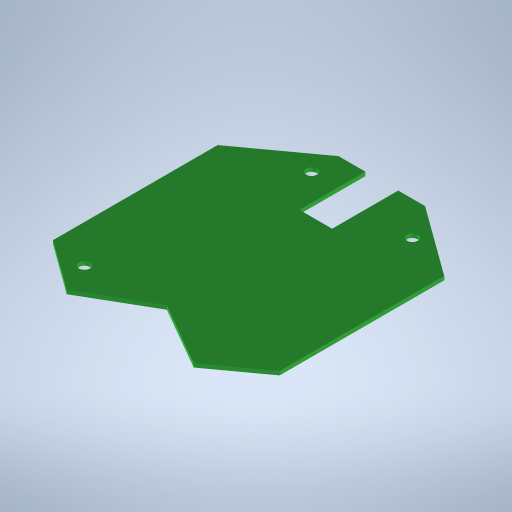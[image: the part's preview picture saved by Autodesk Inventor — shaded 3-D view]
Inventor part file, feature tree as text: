
AUTODESK INVENTOR PART (.ipt)
format: ipt  version: 2024 (Build 280153000, 153)  size: 283,648 bytes
history: native  units: in
note: dims shown in document units (in); Inventor stores cm internally (conversion verified against a paired STEP export)
features: extrude x1, sketch x1
ambient origin geometry x8: Origin, YZ Plane, XZ Plane, XY Plane, X Axis, Y Axis, Z Axis, Center Point
bodies: Solid1 (feature_tree)
feature tree (2):
  extrude  "Extrusion1"  Depth=0.5315in
  sketch  "Sketch1"  dims[d0=2.4803in d1=0.6299in d2=0.0984in d3=0.0669in d4=120.0deg d6=0.0984in d7=0.0669in d8=0.0098in d9=0.0315in d10=0.0in d11=0.2638in d12=0.5315in d13=0.0098in d15=0.0098in d16=0.0098in d24=0.1575in d25=0.0866in d26=0.1575in d27=0.0866in d28=0.1575in d29=0.0866in d30=0.2717in d31=0.3858in d32=0.2165in d33=0.2165in d34=0.3031in d35=0.2402in]
